# Revit family: 205_SIBL-_-1500
name_source: partatom
category: Duct Accessories
units: mm (PartAtom-declared; Revit-internal decimal feet)

## family parameters
Always vertical = Yes
Cut with Voids When Loaded = No
Part Type = Breaks Into
Round Connector Dimension = Use Diameter
Shared = No
Work Plane-Based = No

## types (2) — shared parameters
Description = CIRCULAR SILENCER WITH CORE
L1 = 7 mm  [stored 0.0229659 ft]
L2 = 1486 mm  [stored 4.87533 ft]
L2D = 1500 mm  [stored 4.92126 ft]
LL = 750 mm  [stored 2.46063 ft]
Manufacturer = Alnor
QmdConnectorList = 201;D;202;D
URL = http://www.ventilation-alnor.co.uk
magiPartTypeId = 205
magiProductFamilyId = SIBL-*-1500

## per-type parameters (varying)
| type | CD1 | CD2 | D | H2D | R | W2D |
| SIBL-630-1500 | 400 mm  [stored 1.31234 ft] | 401 mm  [stored 1.31562 ft] | 630 mm | 830 mm | 315 mm  [stored 1.03346 ft] | 830 mm |
| SIBL-800-1500 | 500 mm | 501 mm | 800 mm | 1000 mm  [stored 3.28084 ft] | 400 mm  [stored 1.31234 ft] | 1000 mm  [stored 3.28084 ft] |

note: column(s) folded — value = type name in every type: MC Product Code, magiProductId

note: [stored X ft] marks values corroborated as IEEE doubles in the binary element streams (Revit-internal decimal feet)

## geometry (parser evidence)
native form markers: Blend x4, Sweep x1
no freeform markers — native parametric forms only
